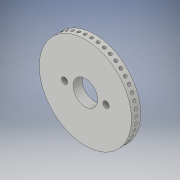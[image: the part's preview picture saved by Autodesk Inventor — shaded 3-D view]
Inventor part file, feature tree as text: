
AUTODESK INVENTOR PART (.ipt)
format: ipt  version: 2017 (Build 210142000, 142)  size: 260,096 bytes
history: native  units: mm
features: extrude x3, sketch x3, other x2, pattern_circular x2
ambient origin geometry x8: Origin, YZ Plane, XZ Plane, XY Plane, X Axis, Y Axis, Z Axis, Center Point
bodies: Body1 (feature_tree)
feature tree (10):
  other  "Твердое тело1"
  extrude  "Выдавливание1"  Depth=8.0mm
  extrude  "Выдавливание2"  Depth=30.0mm
  pattern_circular  "Круговой массив1"  [2 undecoded]
  other  "РабПлоскость1"
  extrude  "Выдавливание4"  Depth=13.5mm
  pattern_circular  "Круговой массив3"  [2 undecoded]
  sketch  "Эскиз1"
  sketch  "Эскиз2"
  sketch  "Эскиз4"
note: 4 required parameter values undecoded (feature->parameter linkage not recoverable at this tier; creation-order binding heuristic only, values carry confidence <= 0.55)
